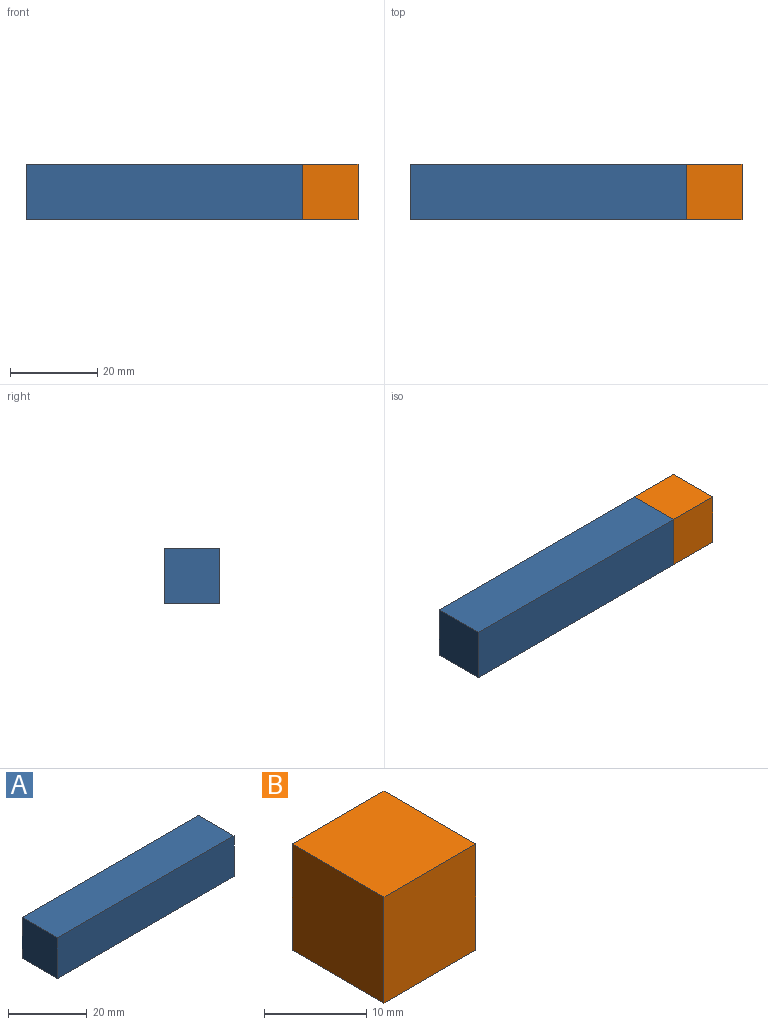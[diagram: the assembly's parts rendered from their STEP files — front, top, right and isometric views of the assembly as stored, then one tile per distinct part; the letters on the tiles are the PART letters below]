
ASSEMBLY  parts=2 mates=1
PART A: 6 faces, bbox 63.5x12.7x12.7 mm
  f0: plane 63.5x12.7mm, normal (0,0,-1), area 806.5mm2, adj f1,f3,f4,f5
  f1: plane 12.7x12.7mm, normal (1,0,0), area 161.3mm2, adj f0,f2,f4,f5
  f2: plane 63.5x12.7mm, normal (0,0,1), area 806.5mm2, adj f1,f3,f4,f5
  f3: plane 12.7x12.7mm, normal (-1,0,0), area 161.3mm2, adj f0,f2,f4,f5
  f4: plane 63.5x12.7mm, normal (0,-1,0), area 806.5mm2, adj f0,f1,f2,f3
  f5: plane 63.5x12.7mm, normal (0,1,0), area 806.5mm2, adj f0,f1,f2,f3
PART B: 6 faces, bbox 12.7x12.7x12.7 mm
  f0: plane 12.7x12.7mm, normal (0,0,-1), area 161.3mm2, adj f1,f3,f4,f5
  f1: plane 12.7x12.7mm, normal (1,0,0), area 161.3mm2, adj f0,f2,f4,f5
  f2: plane 12.7x12.7mm, normal (0,0,1), area 161.3mm2, adj f1,f3,f4,f5
  f3: plane 12.7x12.7mm, normal (-1,0,0), area 161.3mm2, adj f0,f2,f4,f5
  f4: plane 12.7x12.7mm, normal (0,-1,0), area 161.3mm2, adj f0,f1,f2,f3
  f5: plane 12.7x12.7mm, normal (0,1,0), area 161.3mm2, adj f0,f1,f2,f3
PLACE A t=(-31.45,-28.87,20.88)mm
PLACE B t=(3.35,-28.87,-51.3)mm
MATE slider B.f3 <-> A.f1  axis (-1,0,0) through (-3,-35.22,-22.73)mm
